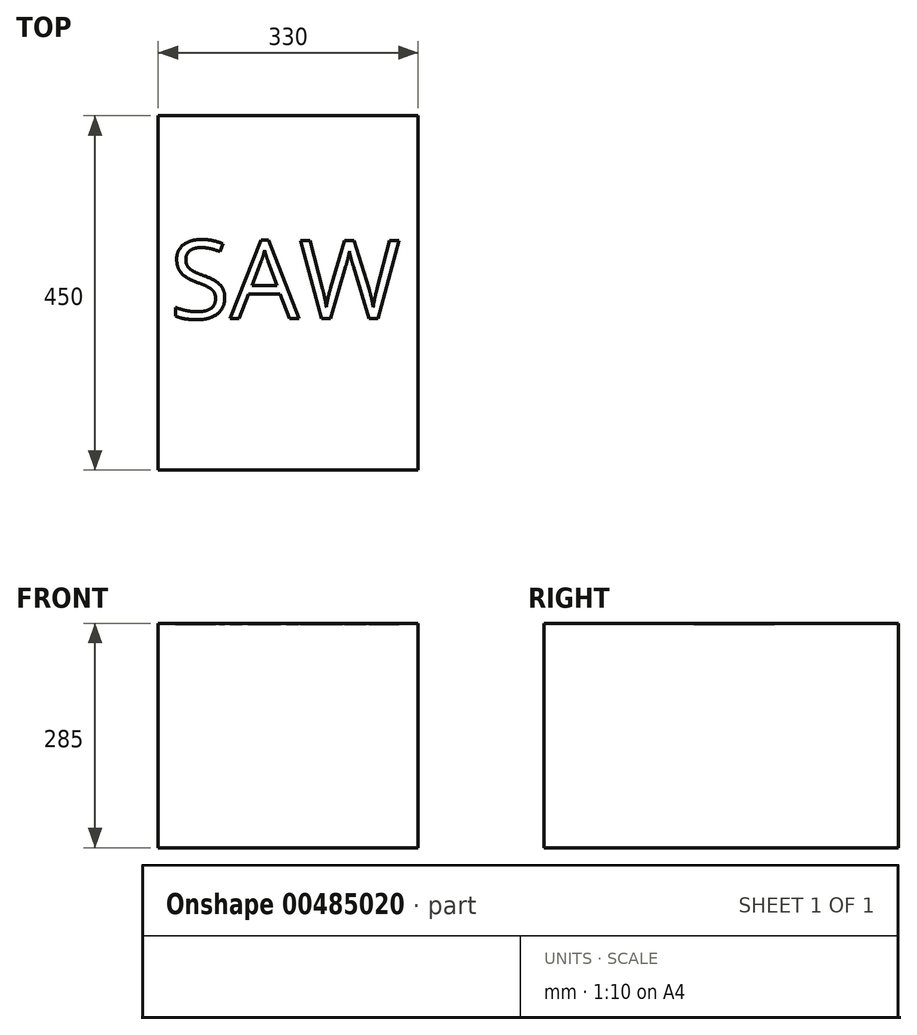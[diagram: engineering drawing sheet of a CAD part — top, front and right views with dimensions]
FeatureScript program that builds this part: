
annotation { "Feature Type Name" : "Feature", "Feature Type Description" : "" }
export const myFeature = defineFeature(function(context is Context, id is Id, definition is map)
    precondition{}
    {
        {
            var Q0;
            Q0=qCreatedBy(makeId("Top.planeOp"),FACE);
            var sketch = newSketch(context, id + "F0", { "sketchPlane" : qUnion([Q0])});
            skLineSegment(sketch, "E0.bottom", {"start": v(-165, -225) * mm, "end": v(165, -225) * mm});
            skLineSegment(sketch, "E0.top", {"start": v(-165, 225) * mm, "end": v(165, 225) * mm});
            skLineSegment(sketch, "E0.left", {"start": v(-165, -225) * mm, "end": v(-165, 225) * mm});
            skLineSegment(sketch, "E0.right", {"start": v(165, -225) * mm, "end": v(165, 225) * mm});
            skPoint(sketch, "E0.middle", {"position": v(0, 0) * mm});
            skSolve(sketch);
        }
        {
            var Q0;
            Q0=makeQuery(id+"F0.imprint","IMPRINT",FACE,{"disambiguationData":[TD([[makeQuery(id+"F0.imprint","IMPRINT",EDGE,{"derivedFrom":sQuery(id+"F0.wireOp",EDGE,"E0.bottom")}),1.0]])]});
            extrude(context, id + "F1", {"entities" : qUnion([Q0]), "depth" : 285 * mm, "offsetDistance" : 25 * mm});
        }
        {
            var Q0;
            Q0=makeQuery(id+"F1.opExtrude","CAP_FACE",FACE,{"disambiguationData":[OSD([sQuery(id+"F0.wireOp",EDGE,"E0.bottom"),sQuery(id+"F0.wireOp",EDGE,"E0.top"),sQuery(id+"F0.wireOp",EDGE,"E0.left"),sQuery(id+"F0.wireOp",EDGE,"E0.right")])],"isStart":false});
            var sketch = newSketch(context, id + "F2", { "sketchPlane" : qUnion([Q0])});
            skText(sketch, "E1", { "text": "SAW\n", "fontName": "OpenSans-Regular.ttf"});
            const initialGuessF2  = {"E1": [-0.15, -0.03278, 1, 0, 0.1]};
            skSetInitialGuess(sketch, initialGuessF2);
            skSolve(sketch);
        }
        {
            var Q0;
            Q0 = qSketchRegion(id + "F2", true);
            extrude(context, id + "F3", {"entities" : qUnion([Q0]), "operationType" : NewBodyOperationType.REMOVE, "oppositeDirection" : true, "depth" : 1 * mm, "offsetDistance" : 25 * mm});
        }
    });
